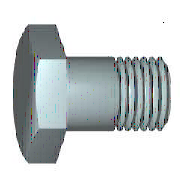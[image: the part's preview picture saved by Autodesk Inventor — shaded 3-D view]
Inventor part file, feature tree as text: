
AUTODESK INVENTOR PART (.ipt)
format: ipt  version: 2019 (Build 230136000, 136)  size: 194,560 bytes
history: native  units: mm (DEFAULTED — no unit token found)
features: sketch x3, extrude x1, chamfer x1, plane x1
ambient origin geometry x7: Origin, YZ Plane, XZ Plane, X Axis, Y Axis, Z Axis, Center Point
bodies: Solid1 (feature_tree), Body (feature_tree)
feature tree (6):
  extrude  "Head"  Depth=37.6mm
  chamfer  "Chamfer1"  Distance=3.0mm
  plane  "Work Plane1"
  sketch  "Sketch1"  dims[d0=40.0mm d1=37.6mm]
  sketch  "Sketch2"  dims[d2=5.0mm]
  sketch  "Sketch4"  dims[d12=90.0deg d3=3.0mm d4=0.0mm d5=30.0deg d21=90.0deg d6=0.49076mm d7=0.49086mm d8=0.0mm d9=0.5001mm d10=8.0mm d11=8.0mm d13=0.49086mm d14=5.0mm d15=37.6mm d16=0.0mm d19=8.0mm d55=45.0deg d57=0.0mm d58=0.0mm]
